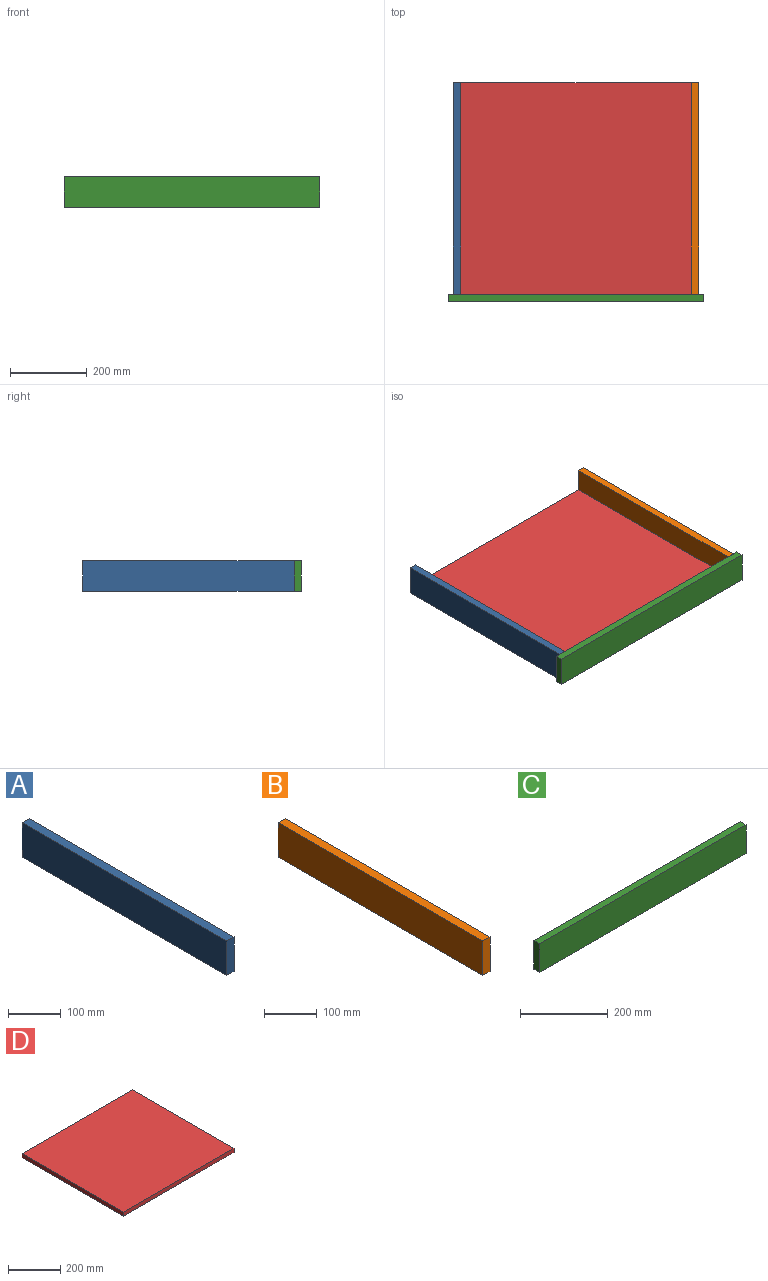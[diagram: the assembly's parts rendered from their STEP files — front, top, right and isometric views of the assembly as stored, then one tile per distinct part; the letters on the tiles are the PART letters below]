
ASSEMBLY  parts=4 mates=3
PART A: 6 faces, bbox 19x550x80 mm
  f0: plane 550x19mm, normal (0,0,1), area 10450mm2, adj f1,f3,f4,f5
  f1: plane 80x19mm, normal (0,-1,0), area 1520mm2, adj f0,f2,f4,f5
  f2: plane 550x19mm, normal (0,0,-1), area 10450mm2, adj f1,f3,f4,f5
  f3: plane 80x19mm, normal (0,1,0), area 1520mm2, adj f0,f2,f4,f5
  f4: plane 550x80mm, normal (1,0,0), area 44000mm2, adj f0,f1,f2,f3
  f5: plane 550x80mm, normal (-1,0,0), area 44000mm2, adj f0,f1,f2,f3
PART B: 6 faces, bbox 19x550x80 mm
  f0: plane 80x19mm, normal (0,1,0), area 1520mm2, adj f1,f3,f4,f5
  f1: plane 550x19mm, normal (0,0,1), area 10450mm2, adj f0,f2,f4,f5
  f2: plane 80x19mm, normal (0,-1,0), area 1520mm2, adj f1,f3,f4,f5
  f3: plane 550x19mm, normal (0,0,-1), area 10450mm2, adj f0,f2,f4,f5
  f4: plane 550x80mm, normal (1,0,0), area 44000mm2, adj f0,f1,f2,f3
  f5: plane 550x80mm, normal (-1,0,0), area 44000mm2, adj f0,f1,f2,f3
PART C: 6 faces, bbox 664x19x80 mm
  f0: plane 664x19mm, normal (0,0,1), area 12616mm2, adj f1,f3,f4,f5
  f1: plane 80x19mm, normal (-1,0,0), area 1520mm2, adj f0,f2,f4,f5
  f2: plane 664x19mm, normal (0,0,-1), area 12616mm2, adj f1,f3,f4,f5
  f3: plane 80x19mm, normal (1,0,0), area 1520mm2, adj f0,f2,f4,f5
  f4: plane 664x80mm, normal (0,-1,0), area 53120mm2, adj f0,f1,f2,f3
  f5: plane 664x80mm, normal (0,1,0), area 53120mm2, adj f0,f1,f2,f3
PART D: 6 faces, bbox 600x550x19 mm
  f0: plane 550x19mm, normal (1,0,0), area 10450mm2, adj f1,f3,f4,f5
  f1: plane 600x19mm, normal (0,1,0), area 11400mm2, adj f0,f2,f4,f5
  f2: plane 550x19mm, normal (-1,0,0), area 10450mm2, adj f1,f3,f4,f5
  f3: plane 600x19mm, normal (0,-1,0), area 11400mm2, adj f0,f2,f4,f5
  f4: plane 600x550mm, normal (0,0,1), area 330000mm2, adj f0,f1,f2,f3
  f5: plane 600x550mm, normal (0,0,-1), area 330000mm2, adj f0,f1,f2,f3
PLACE A t=(-480.14,-24.23,107.64)mm
PLACE B t=(138.86,-54.2,107.64)mm
PLACE C t=(-161.14,-318.58,107.64)mm
PLACE D t=(-161.14,-43.58,67.64)mm
MATE fastened C.f5 <-> D.f3  axis (0,1,0) through (-161.14,-318.58,67.64)mm
MATE fastened A.f4 <-> D.f2  axis (1,0,0) through (-461.14,-318.58,67.64)mm
MATE fastened B.f5 <-> D.f0  axis (-1,0,0) through (138.86,-318.58,67.64)mm
